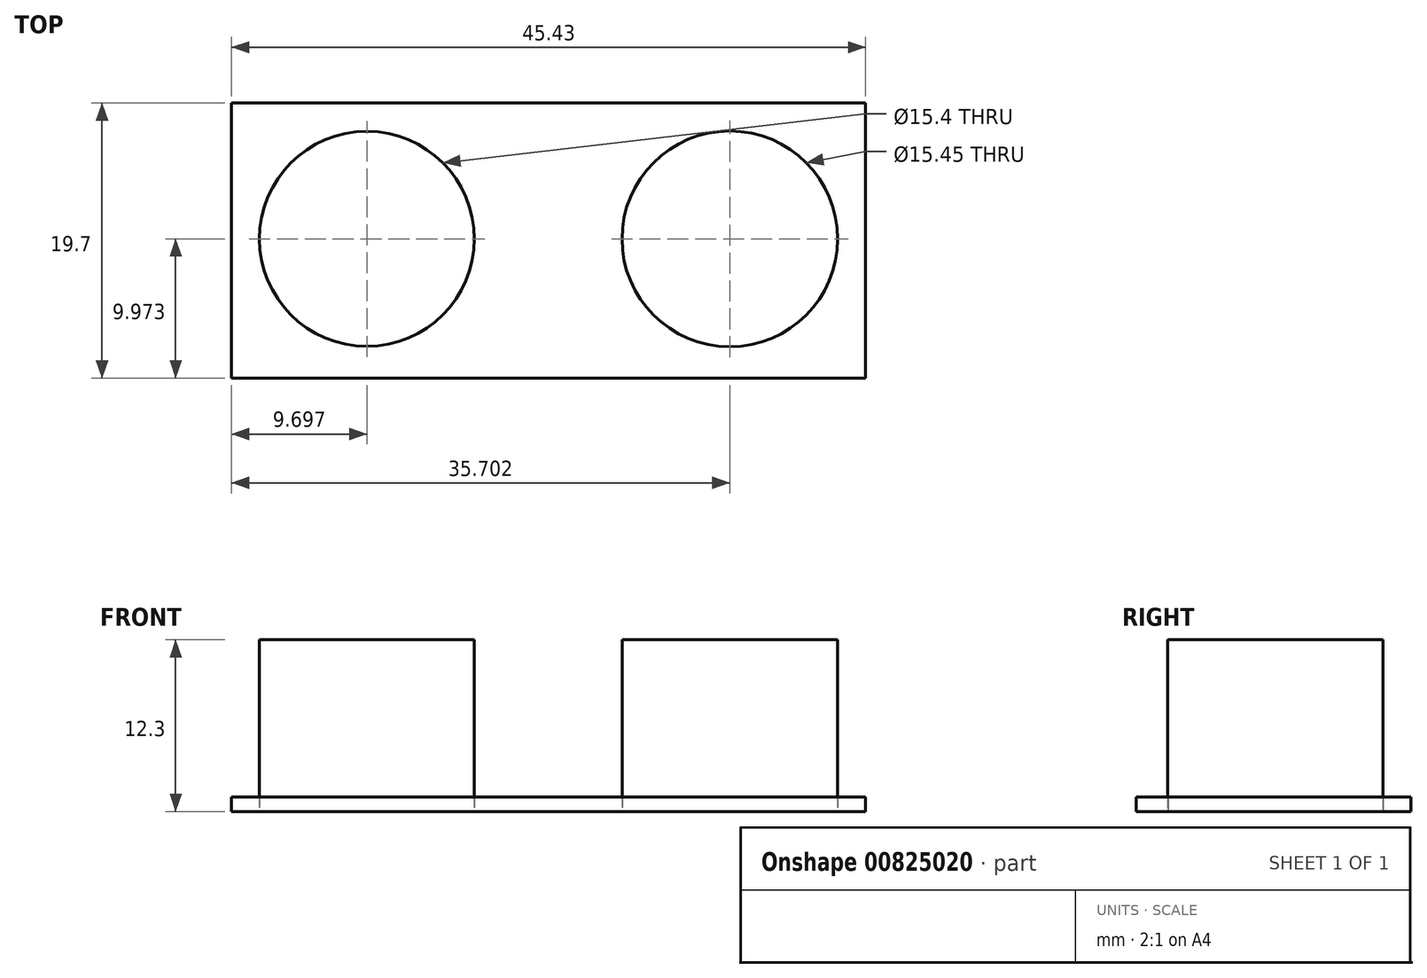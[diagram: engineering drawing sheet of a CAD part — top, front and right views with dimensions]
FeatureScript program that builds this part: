
annotation { "Feature Type Name" : "Feature", "Feature Type Description" : "" }
export const myFeature = defineFeature(function(context is Context, id is Id, definition is map)
    precondition{}
    {
        {
            var Q0;
            Q0=qCreatedBy(makeId("Top.planeOp"),FACE);
            var sketch = newSketch(context, id + "F0", { "sketchPlane" : qUnion([Q0])});
            skLineSegment(sketch, "E0", {"start": v(-43.72, 12.2) * mm, "end": v(-43.72, -7.5) * mm});
            skLineSegment(sketch, "E1", {"start": v(-43.72, -7.5) * mm, "end": v(1.7, -7.5) * mm});
            skLineSegment(sketch, "E2", {"start": v(1.7, -7.5) * mm, "end": v(1.7, 12.2) * mm});
            skLineSegment(sketch, "E3", {"start": v(1.7, 12.2) * mm, "end": v(-43.72, 12.2) * mm});
            skCircle(sketch, "E4", {"center": v(-34.02, 2.47) * mm, "radius": 7.7 * mm});
            skCircle(sketch, "E5", {"center": v(-8.02, 2.47) * mm, "radius": 7.73 * mm});
            skSolve(sketch);
        }
        {
            var Q0;
            Q0=makeQuery(id+"F0.imprint","IMPRINT",FACE,{"disambiguationData":[TD([[makeQuery(id+"F0.imprint","IMPRINT",EDGE,{"derivedFrom":sQuery(id+"F0.wireOp",EDGE,"E4")}),1.0]])]});
            var Q1;
            Q1=makeQuery(id+"F0.imprint","IMPRINT",FACE,{"disambiguationData":[TD([[makeQuery(id+"F0.imprint","IMPRINT",EDGE,{"derivedFrom":sQuery(id+"F0.wireOp",EDGE,"E5")}),1.0]])]});
            extrude(context, id + "F1", {"entities" : qUnion([Q0, Q1]), "depth" : 12.3 * mm, "offsetDistance" : 25.4 * mm});
        }
        {
            var Q0;
            Q0 = qSketchRegion(id + "F0", true);
            extrude(context, id + "F2", {"entities" : qUnion([Q0]), "depth" : 1.03 * mm, "offsetDistance" : 25.4 * mm});
        }
    });
